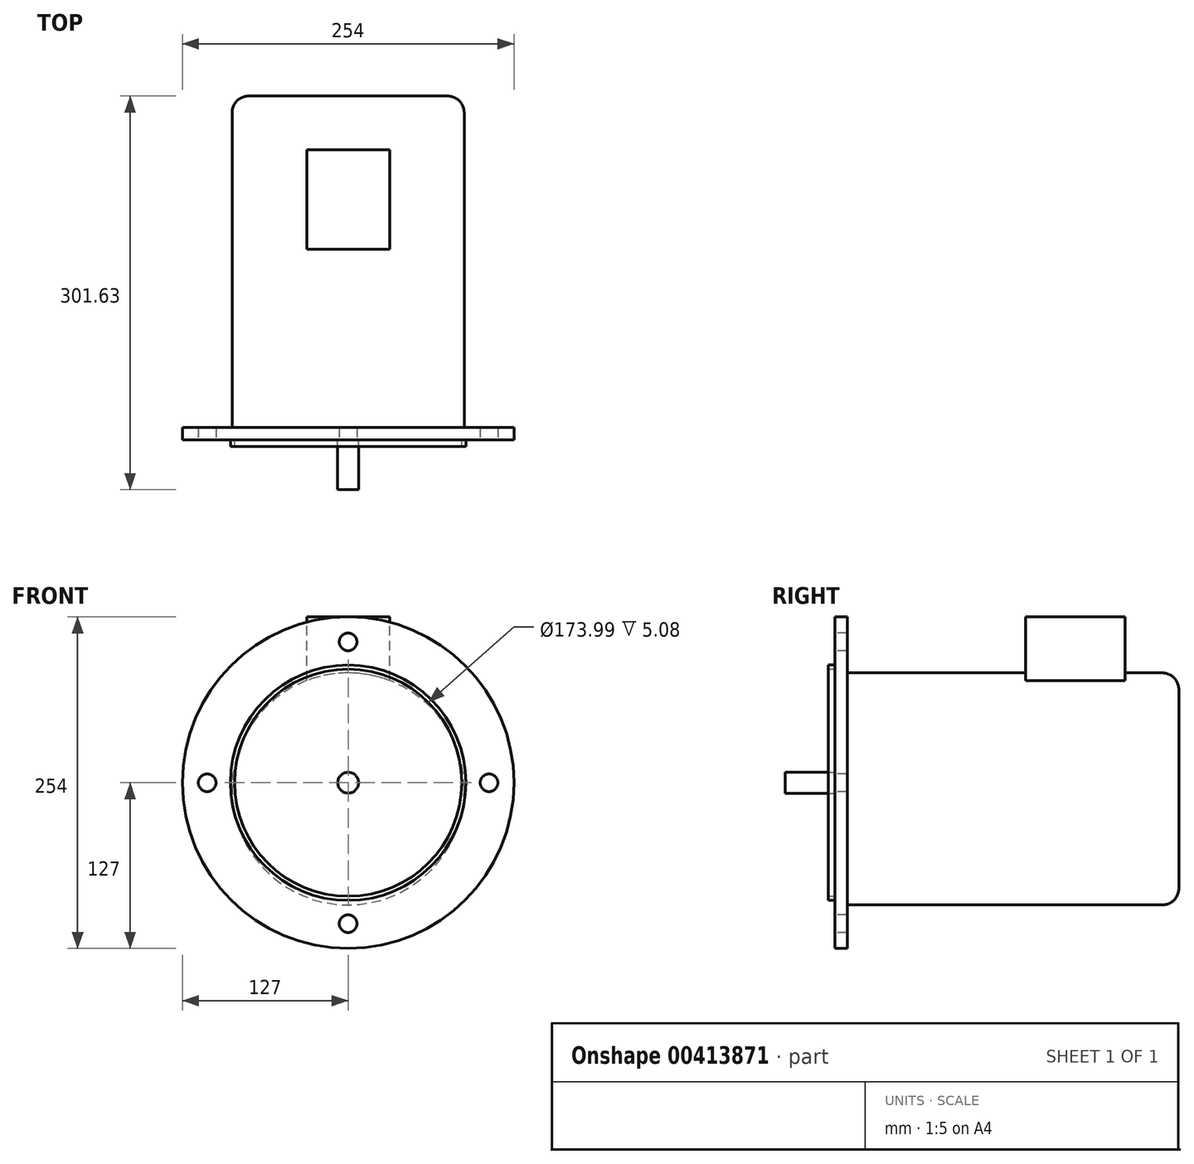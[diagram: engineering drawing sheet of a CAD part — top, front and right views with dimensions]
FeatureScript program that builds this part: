
annotation { "Feature Type Name" : "Feature", "Feature Type Description" : "" }
export const myFeature = defineFeature(function(context is Context, id is Id, definition is map)
    precondition{}
    {
        {
            var Q0;
            Q0=qCreatedBy(makeId("Front.planeOp"),FACE);
            var sketch = newSketch(context, id + "F0", { "sketchPlane" : qUnion([Q0])});
            skCircle(sketch, "E0", {"center": v(0, 0) * mm, "radius": 127 * mm});
            skSolve(sketch);
        }
        {
            var Q0;
            Q0 = qSketchRegion(id + "F0", true);
            extrude(context, id + "F1", {"entities" : qUnion([Q0]), "oppositeDirection" : true, "depth" : 9.52 * mm});
        }
        {
            var Q0;
            Q0=makeQuery(id+"F1.opExtrude","CAP_FACE",FACE,{"disambiguationData":[OSD([sQuery(id+"F0.wireOp",EDGE,"E0")])],"isStart":false});
            var sketch = newSketch(context, id + "F2", { "sketchPlane" : qUnion([Q0])});
            skCircle(sketch, "E1", {"center": v(0, -4.74) * mm, "radius": 88.9 * mm});
            skSolve(sketch);
        }
        {
            var Q0;
            Q0 = qSketchRegion(id + "F2", true);
            extrude(context, id + "F3", {"entities" : qUnion([Q0]), "operationType" : NewBodyOperationType.ADD, "depth" : 254 * mm});
        }
        {
            var Q0;
            Q0=qCreatedBy(makeId("Top.planeOp"),FACE);
            cPlane(context, id + "F4", {"entities" : qUnion([Q0]), "cplaneType" : CPlaneType.OFFSET, "offset" : 127 * mm, "width" : 152.4 * mm, "height" : 152.4 * mm});
        }
        {
            var Q0;
            Q0=qCreatedBy(id+"F4.planeOp",FACE);
            var sketch = newSketch(context, id + "F5", { "sketchPlane" : qUnion([Q0])});
            skLineSegment(sketch, "E2.bottom", {"start": v(31.75, 146.26) * mm, "end": v(-31.75, 146.26) * mm});
            skLineSegment(sketch, "E2.top", {"start": v(31.75, 222.46) * mm, "end": v(-31.75, 222.46) * mm});
            skLineSegment(sketch, "E2.left", {"start": v(31.75, 146.26) * mm, "end": v(31.75, 222.46) * mm});
            skLineSegment(sketch, "E2.right", {"start": v(-31.75, 146.26) * mm, "end": v(-31.75, 222.46) * mm});
            skPoint(sketch, "E2.middle", {"position": v(0, 184.36) * mm});
            skSolve(sketch);
        }
        {
            var Q0;
            Q0 = qSketchRegion(id + "F5", true);
            extrude(context, id + "F6", {"entities" : qUnion([Q0]), "operationType" : NewBodyOperationType.ADD, "oppositeDirection" : true, "depth" : 76.2 * mm});
        }
        {
            var Q0;
            Q0=makeQuery(id+"F1.opExtrude","CAP_FACE",FACE,{"disambiguationData":[OSD([sQuery(id+"F0.wireOp",EDGE,"E0")])],"isStart":true});
            var sketch = newSketch(context, id + "F7", { "sketchPlane" : qUnion([Q0])});
            skCircle(sketch, "E3", {"center": v(0, 0) * mm, "radius": 107.95 * mm, "construction": true});
            skCircle(sketch, "E4", {"center": v(107.95, 0) * mm, "radius": 6.75 * mm});
            skCircle(sketch, "E5.1.0", {"center": v(0, 107.95) * mm, "radius": 6.75 * mm});
            skCircle(sketch, "E5.2.0", {"center": v(-107.95, 0) * mm, "radius": 6.75 * mm});
            skCircle(sketch, "E5.3.0", {"center": v(0, -107.95) * mm, "radius": 6.75 * mm});
            skSolve(sketch);
        }
        {
            var Q0;
            Q0 = qSketchRegion(id + "F7", true);
            extrude(context, id + "F8", {"entities" : qUnion([Q0]), "operationType" : NewBodyOperationType.REMOVE, "oppositeDirection" : true, "depth" : 25.4 * mm});
        }
        {
            var Q0;
            Q0=makeQuery(id+"F3.opExtrude","CAP_EDGE",EDGE,{"disambiguationData":[OSD([sQuery(id+"F2.wireOp",EDGE,"E1")])],"isStart":false});
            fillet(context, id + "F9", {"entities" : qUnion([Q0]), "radius" : 12.7 * mm, "tangentPropagation" : true, "allowEdgeOverflow" : false});
        }
        {
            var Q0;
            Q0=makeQuery(id+"F1.opExtrude","CAP_FACE",FACE,{"disambiguationData":[OSD([sQuery(id+"F0.wireOp",EDGE,"E0")])],"isStart":true});
            var sketch = newSketch(context, id + "F10", { "sketchPlane" : qUnion([Q0])});
            skCircle(sketch, "E6", {"center": v(0, 0) * mm, "radius": 90.17 * mm});
            skCircle(sketch, "E7.0", {"center": v(0, 0) * mm, "radius": 87 * mm});
            skSolve(sketch);
        }
        {
            var Q0;
            Q0 = qSketchRegion(id + "F10", true);
            extrude(context, id + "F11", {"entities" : qUnion([Q0]), "operationType" : NewBodyOperationType.ADD, "depth" : 5.08 * mm});
        }
        {
            var Q0;
            Q0=makeQuery(id+"F11.boolean.opBoolean","SPLIT",FACE,{"disambiguationData":[TD([makeQuery(id+"F11.opExtrude","SWEPT_FACE",FACE,{"disambiguationData":[OSD([sQuery(id+"F10.wireOp",EDGE,"E7.0")])]})])],"derivedFrom":makeQuery(id+"F1.opExtrude","CAP_FACE",FACE,{"disambiguationData":[OSD([sQuery(id+"F0.wireOp",EDGE,"E0")])],"isStart":true})});
            var sketch = newSketch(context, id + "F12", { "sketchPlane" : qUnion([Q0])});
            skCircle(sketch, "E8", {"center": v(0, 0) * mm, "radius": 8 * mm});
            skSolve(sketch);
        }
        {
            var Q0;
            Q0 = qSketchRegion(id + "F12", true);
            extrude(context, id + "F13", {"entities" : qUnion([Q0]), "operationType" : NewBodyOperationType.ADD, "depth" : 38.1 * mm});
        }
    });
